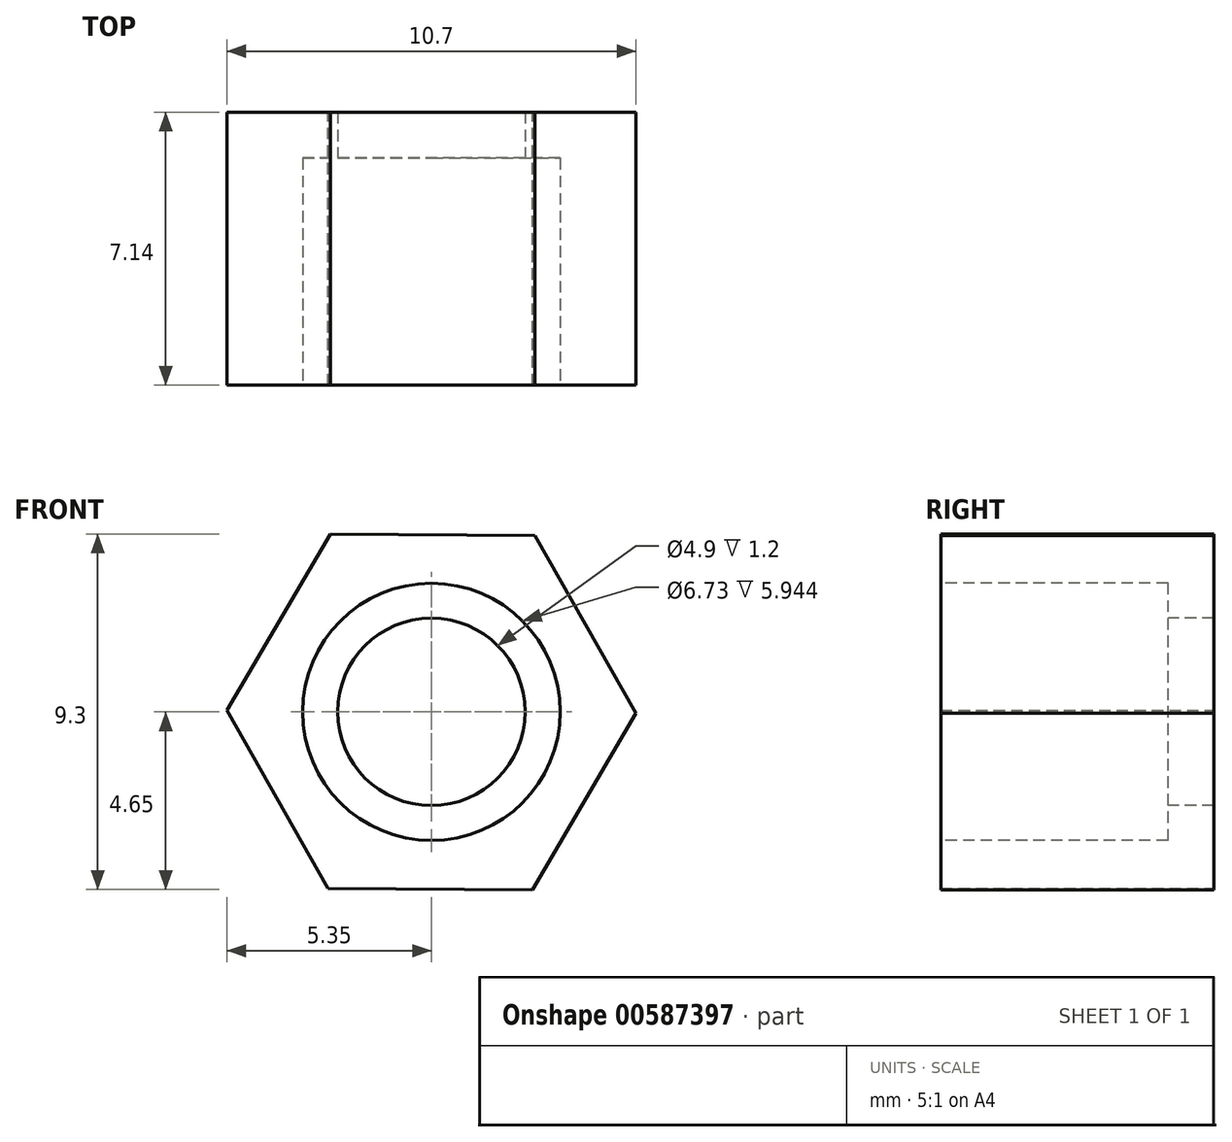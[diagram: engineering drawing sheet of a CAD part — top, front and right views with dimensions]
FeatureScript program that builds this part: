
annotation { "Feature Type Name" : "Feature", "Feature Type Description" : "" }
export const myFeature = defineFeature(function(context is Context, id is Id, definition is map)
    precondition{}
    {
        {
            var Q0;
            Q0=qCreatedBy(makeId("Front.planeOp"),FACE);
            var sketch = newSketch(context, id + "F0", { "sketchPlane" : qUnion([Q0])});
            skLineSegment(sketch, "E0", {"start": v(0, 53.14) * mm, "end": v(0, -54.33) * mm, "construction": true});
            skLineSegment(sketch, "E1", {"start": v(60.88, 0) * mm, "end": v(-66.03, 0) * mm, "construction": true});
            skLineSegment(sketch, "E2", {"start": v(-27.96, 32.92) * mm, "end": v(29.55, 32.92) * mm});
            skLineSegment(sketch, "E3", {"start": v(-27.17, -30.54) * mm, "end": v(29.55, -30.54) * mm});
            skCircle(sketch, "E4.cCircle", {"center": v(0, 0) * mm, "radius": 4.64 * mm, "construction": true});
            skLineSegment(sketch, "E4.0", {"start": v(-5.35, 0.04) * mm, "end": v(-2.64, 4.65) * mm});
            skLineSegment(sketch, "E4.1", {"start": v(-2.64, 4.65) * mm, "end": v(2.7, 4.62) * mm});
            skLineSegment(sketch, "E4.2", {"start": v(2.7, 4.62) * mm, "end": v(5.35, -0.04) * mm});
            skLineSegment(sketch, "E4.3", {"start": v(5.35, -0.04) * mm, "end": v(2.64, -4.65) * mm});
            skLineSegment(sketch, "E4.4", {"start": v(2.64, -4.65) * mm, "end": v(-2.7, -4.62) * mm});
            skLineSegment(sketch, "E4.5", {"start": v(-2.7, -4.62) * mm, "end": v(-5.35, 0.04) * mm});
            skPoint(sketch, "E4.0.midPoint", {"position": v(-4, 2.35) * mm});
            skSolve(sketch);
        }
        {
            var Q0;
            Q0=makeQuery(id+"F0.imprint","IMPRINT",FACE,{"disambiguationData":[TD([[makeQuery(id+"F0.imprint","IMPRINT",EDGE,{"derivedFrom":sQuery(id+"F0.wireOp",EDGE,"E4.0")}),-1.0]])]});
            extrude(context, id + "F1", {"entities" : qUnion([Q0]), "depth" : 7.14 * mm, "offsetDistance" : 25.4 * mm});
        }
        {
            var Q0;
            Q0=makeQuery(id+"F1.opExtrude","CAP_FACE",FACE,{"disambiguationData":[OSD([sQuery(id+"F0.wireOp",EDGE,"E4.0"),sQuery(id+"F0.wireOp",EDGE,"E4.1"),sQuery(id+"F0.wireOp",EDGE,"E4.2"),sQuery(id+"F0.wireOp",EDGE,"E4.3"),sQuery(id+"F0.wireOp",EDGE,"E4.4"),sQuery(id+"F0.wireOp",EDGE,"E4.5")])],"isStart":false});
            var sketch = newSketch(context, id + "F2", { "sketchPlane" : qUnion([Q0])});
            skCircle(sketch, "E5", {"center": v(0, 0) * mm, "radius": 2.45 * mm});
            skSolve(sketch);
        }
        {
            var Q0;
            Q0=makeQuery(id+"F2.imprint","IMPRINT",FACE,{"disambiguationData":[TD([[makeQuery(id+"F2.imprint","IMPRINT",EDGE,{"derivedFrom":sQuery(id+"F2.wireOp",EDGE,"E5")}),1.0]])]});
            extrude(context, id + "F3", {"entities" : qUnion([Q0]), "operationType" : NewBodyOperationType.REMOVE, "endBound" : BoundingType.THROUGH_ALL, "oppositeDirection" : true, "depth" : 25.4 * mm, "offsetDistance" : 25.4 * mm});
        }
        {
            var Q0;
            Q0=makeQuery(id+"F1.opExtrude","CAP_FACE",FACE,{"disambiguationData":[OSD([sQuery(id+"F0.wireOp",EDGE,"E4.0"),sQuery(id+"F0.wireOp",EDGE,"E4.1"),sQuery(id+"F0.wireOp",EDGE,"E4.2"),sQuery(id+"F0.wireOp",EDGE,"E4.3"),sQuery(id+"F0.wireOp",EDGE,"E4.4"),sQuery(id+"F0.wireOp",EDGE,"E4.5")])],"isStart":false});
            var sketch = newSketch(context, id + "F4", { "sketchPlane" : qUnion([Q0])});
            skCircle(sketch, "E6", {"center": v(0, 0) * mm, "radius": 3.37 * mm});
            skSolve(sketch);
        }
        {
            var Q0;
            Q0=makeQuery(id+"F4.imprint","IMPRINT",FACE,{"disambiguationData":[TD([[makeQuery(id+"F4.imprint","IMPRINT",EDGE,{"derivedFrom":sQuery(id+"F4.wireOp",EDGE,"E6")}),1.0]])]});
            extrude(context, id + "F5", {"entities" : qUnion([Q0]), "operationType" : NewBodyOperationType.REMOVE, "oppositeDirection" : true, "depth" : 5.94 * mm, "offsetDistance" : 25.4 * mm});
        }
    });
